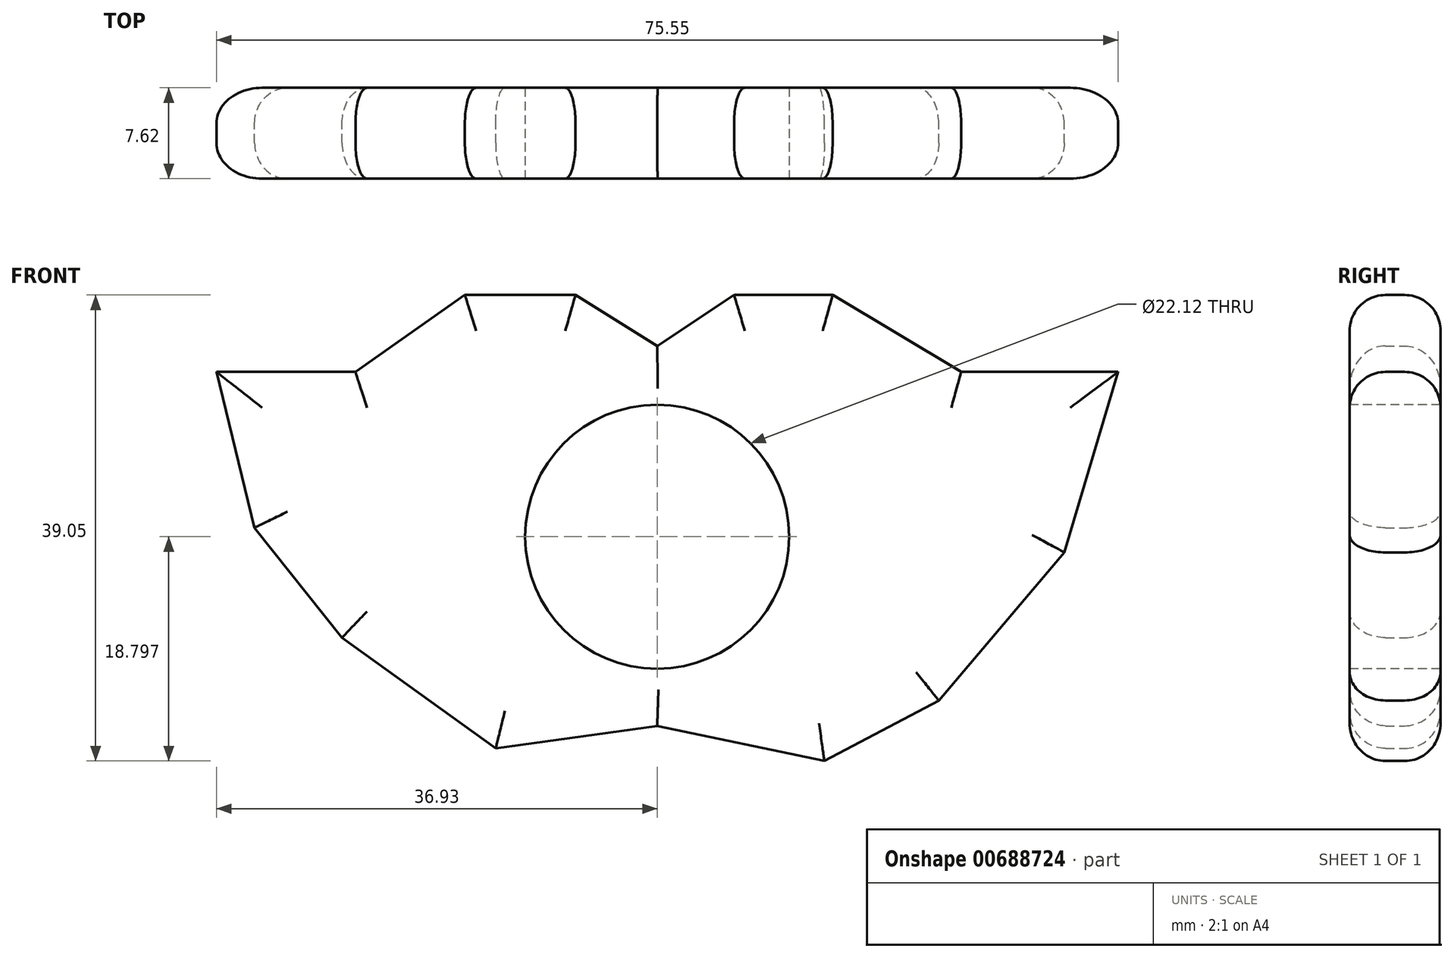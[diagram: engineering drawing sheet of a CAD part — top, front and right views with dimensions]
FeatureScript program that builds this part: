
annotation { "Feature Type Name" : "Feature", "Feature Type Description" : "" }
export const myFeature = defineFeature(function(context is Context, id is Id, definition is map)
    precondition{}
    {
        {
            var Q0;
            Q0=qCreatedBy(makeId("Front.planeOp"),FACE);
            var sketch = newSketch(context, id + "F0", { "sketchPlane" : qUnion([Q0])});
            skLineSegment(sketch, "E0", {"start": v(-6.84, 6.44) * mm, "end": v(0, 2.18) * mm});
            skLineSegment(sketch, "E1", {"start": v(0, 2.18) * mm, "end": v(6.44, 6.44) * mm});
            skLineSegment(sketch, "E2", {"start": v(-25.28, 0) * mm, "end": v(-36.93, 0) * mm});
            skLineSegment(sketch, "E3", {"start": v(-36.93, 0) * mm, "end": v(-33.74, -13.06) * mm});
            skLineSegment(sketch, "E4", {"start": v(-25.28, 0) * mm, "end": v(-16.12, 6.44) * mm});
            skLineSegment(sketch, "E5", {"start": v(-16.12, 6.44) * mm, "end": v(-6.84, 6.44) * mm});
            skLineSegment(sketch, "E6", {"start": v(6.44, 6.44) * mm, "end": v(14.7, 6.44) * mm});
            skLineSegment(sketch, "E7", {"start": v(14.7, 6.44) * mm, "end": v(25.47, 0) * mm});
            skLineSegment(sketch, "E8", {"start": v(38.62, 0) * mm, "end": v(34.11, -15.13) * mm});
            skLineSegment(sketch, "E9", {"start": v(-33.74, -13.06) * mm, "end": v(-26.4, -22.27) * mm});
            skLineSegment(sketch, "E10", {"start": v(-26.4, -22.27) * mm, "end": v(-13.54, -31.56) * mm});
            skLineSegment(sketch, "E11", {"start": v(34.11, -15.13) * mm, "end": v(23.59, -27.53) * mm});
            skLineSegment(sketch, "E12", {"start": v(23.59, -27.53) * mm, "end": v(14, -32.6) * mm});
            skLineSegment(sketch, "E13", {"start": v(14, -32.6) * mm, "end": v(0, -29.66) * mm});
            skLineSegment(sketch, "E14", {"start": v(0, -29.66) * mm, "end": v(-13.54, -31.56) * mm});
            skLineSegment(sketch, "E15", {"start": v(25.47, 0) * mm, "end": v(38.62, 0) * mm});
            skSolve(sketch);
        }
        {
            var Q0;
            Q0 = qSketchRegion(id + "F0", true);
            extrude(context, id + "F1", {"entities" : qUnion([Q0]), "depth" : 7.62 * mm, "offsetDistance" : 25.4 * mm});
        }
        {
            var Q0;
            Q0=makeQuery(id+"F1.opExtrude","CAP_FACE",FACE,{"disambiguationData":[OSD([sQuery(id+"F0.wireOp",EDGE,"E0"),sQuery(id+"F0.wireOp",EDGE,"E1"),sQuery(id+"F0.wireOp",EDGE,"E2"),sQuery(id+"F0.wireOp",EDGE,"E3"),sQuery(id+"F0.wireOp",EDGE,"E4"),sQuery(id+"F0.wireOp",EDGE,"E5"),sQuery(id+"F0.wireOp",EDGE,"E6"),sQuery(id+"F0.wireOp",EDGE,"E7"),sQuery(id+"F0.wireOp",EDGE,"bgftpzii-J6rh-5dA1-gnNM-FfCZ00Urv5oc"),sQuery(id+"F0.wireOp",EDGE,"E8"),sQuery(id+"F0.wireOp",EDGE,"E9"),sQuery(id+"F0.wireOp",EDGE,"E10"),sQuery(id+"F0.wireOp",EDGE,"E11"),sQuery(id+"F0.wireOp",EDGE,"E12"),sQuery(id+"F0.wireOp",EDGE,"E13"),sQuery(id+"F0.wireOp",EDGE,"E14")])],"isStart":false});
            var sketch = newSketch(context, id + "F2", { "sketchPlane" : qUnion([Q0])});
            skCircle(sketch, "E16", {"center": v(0, -13.81) * mm, "radius": 11.06 * mm});
            skCircle(sketch, "E17", {"center": v(0, -13.81) * mm, "radius": 13 * mm});
            skSolve(sketch);
        }
        {
            var Q0;
            Q0=makeQuery(id+"F2.imprint","IMPRINT",FACE,{"disambiguationData":[TD([[makeQuery(id+"F2.imprint","IMPRINT",EDGE,{"derivedFrom":sQuery(id+"F2.wireOp",EDGE,"E16")}),1.0]])]});
            extrude(context, id + "F3", {"entities" : qUnion([Q0]), "operationType" : NewBodyOperationType.REMOVE, "oppositeDirection" : true, "depth" : 10 * mm, "offsetDistance" : 25.4 * mm});
        }
        {
            var Q0;
            Q0=makeQuery(id+"F1.opExtrude","CAP_EDGE",EDGE,{"disambiguationData":[OSD([sQuery(id+"F0.wireOp",EDGE,"E3")])],"isStart":false});
            var Q1;
            Q1=makeQuery(id+"F1.opExtrude","CAP_EDGE",EDGE,{"disambiguationData":[OSD([sQuery(id+"F0.wireOp",EDGE,"E9")])],"isStart":false});
            var Q2;
            Q2=makeQuery(id+"F1.opExtrude","CAP_EDGE",EDGE,{"disambiguationData":[OSD([sQuery(id+"F0.wireOp",EDGE,"E10")])],"isStart":false});
            var Q3;
            Q3=makeQuery(id+"F1.opExtrude","CAP_EDGE",EDGE,{"disambiguationData":[OSD([sQuery(id+"F0.wireOp",EDGE,"E14")])],"isStart":false});
            var Q4;
            Q4=makeQuery(id+"F1.opExtrude","CAP_EDGE",EDGE,{"disambiguationData":[OSD([sQuery(id+"F0.wireOp",EDGE,"E13")])],"isStart":false});
            var Q5;
            Q5=makeQuery(id+"F1.opExtrude","CAP_EDGE",EDGE,{"disambiguationData":[OSD([sQuery(id+"F0.wireOp",EDGE,"E12")])],"isStart":false});
            var Q6;
            Q6=makeQuery(id+"F1.opExtrude","CAP_EDGE",EDGE,{"disambiguationData":[OSD([sQuery(id+"F0.wireOp",EDGE,"E11")])],"isStart":false});
            var Q7;
            Q7=makeQuery(id+"F1.opExtrude","CAP_EDGE",EDGE,{"disambiguationData":[OSD([sQuery(id+"F0.wireOp",EDGE,"E8")])],"isStart":false});
            var Q8;
            Q8=makeQuery(id+"F1.opExtrude","CAP_EDGE",EDGE,{"disambiguationData":[OSD([sQuery(id+"F0.wireOp",EDGE,"E15")])],"isStart":false});
            var Q9;
            Q9=makeQuery(id+"F1.opExtrude","CAP_EDGE",EDGE,{"disambiguationData":[OSD([sQuery(id+"F0.wireOp",EDGE,"E7")])],"isStart":false});
            var Q10;
            Q10=makeQuery(id+"F1.opExtrude","CAP_EDGE",EDGE,{"disambiguationData":[OSD([sQuery(id+"F0.wireOp",EDGE,"E6")])],"isStart":false});
            var Q11;
            Q11=makeQuery(id+"F1.opExtrude","CAP_EDGE",EDGE,{"disambiguationData":[OSD([sQuery(id+"F0.wireOp",EDGE,"E1")])],"isStart":false});
            var Q12;
            Q12=makeQuery(id+"F1.opExtrude","CAP_EDGE",EDGE,{"disambiguationData":[OSD([sQuery(id+"F0.wireOp",EDGE,"E0")])],"isStart":false});
            var Q13;
            Q13=makeQuery(id+"F1.opExtrude","CAP_EDGE",EDGE,{"disambiguationData":[OSD([sQuery(id+"F0.wireOp",EDGE,"E5")])],"isStart":false});
            var Q14;
            Q14=makeQuery(id+"F1.opExtrude","CAP_EDGE",EDGE,{"disambiguationData":[OSD([sQuery(id+"F0.wireOp",EDGE,"E4")])],"isStart":false});
            var Q15;
            Q15=makeQuery(id+"F1.opExtrude","CAP_EDGE",EDGE,{"disambiguationData":[OSD([sQuery(id+"F0.wireOp",EDGE,"E2")])],"isStart":false});
            var Q16;
            Q16=makeQuery(id+"F1.opExtrude","CAP_EDGE",EDGE,{"disambiguationData":[OSD([sQuery(id+"F0.wireOp",EDGE,"E2")])],"isStart":true});
            var Q17;
            Q17=makeQuery(id+"F1.opExtrude","CAP_EDGE",EDGE,{"disambiguationData":[OSD([sQuery(id+"F0.wireOp",EDGE,"E3")])],"isStart":true});
            var Q18;
            Q18=makeQuery(id+"F1.opExtrude","CAP_EDGE",EDGE,{"disambiguationData":[OSD([sQuery(id+"F0.wireOp",EDGE,"E9")])],"isStart":true});
            var Q19;
            Q19=makeQuery(id+"F1.opExtrude","CAP_EDGE",EDGE,{"disambiguationData":[OSD([sQuery(id+"F0.wireOp",EDGE,"E10")])],"isStart":true});
            var Q20;
            Q20=makeQuery(id+"F1.opExtrude","CAP_EDGE",EDGE,{"disambiguationData":[OSD([sQuery(id+"F0.wireOp",EDGE,"E14")])],"isStart":true});
            var Q21;
            Q21=makeQuery(id+"F1.opExtrude","CAP_EDGE",EDGE,{"disambiguationData":[OSD([sQuery(id+"F0.wireOp",EDGE,"E13")])],"isStart":true});
            var Q22;
            Q22=makeQuery(id+"F1.opExtrude","CAP_EDGE",EDGE,{"disambiguationData":[OSD([sQuery(id+"F0.wireOp",EDGE,"E12")])],"isStart":true});
            var Q23;
            Q23=makeQuery(id+"F1.opExtrude","CAP_EDGE",EDGE,{"disambiguationData":[OSD([sQuery(id+"F0.wireOp",EDGE,"E11")])],"isStart":true});
            var Q24;
            Q24=makeQuery(id+"F1.opExtrude","CAP_EDGE",EDGE,{"disambiguationData":[OSD([sQuery(id+"F0.wireOp",EDGE,"E8")])],"isStart":true});
            var Q25;
            Q25=makeQuery(id+"F1.opExtrude","CAP_EDGE",EDGE,{"disambiguationData":[OSD([sQuery(id+"F0.wireOp",EDGE,"E15")])],"isStart":true});
            var Q26;
            Q26=makeQuery(id+"F1.opExtrude","CAP_EDGE",EDGE,{"disambiguationData":[OSD([sQuery(id+"F0.wireOp",EDGE,"E7")])],"isStart":true});
            var Q27;
            Q27=makeQuery(id+"F1.opExtrude","CAP_EDGE",EDGE,{"disambiguationData":[OSD([sQuery(id+"F0.wireOp",EDGE,"E6")])],"isStart":true});
            var Q28;
            Q28=makeQuery(id+"F1.opExtrude","CAP_EDGE",EDGE,{"disambiguationData":[OSD([sQuery(id+"F0.wireOp",EDGE,"E1")])],"isStart":true});
            var Q29;
            Q29=makeQuery(id+"F1.opExtrude","CAP_EDGE",EDGE,{"disambiguationData":[OSD([sQuery(id+"F0.wireOp",EDGE,"E0")])],"isStart":true});
            var Q30;
            Q30=makeQuery(id+"F1.opExtrude","CAP_EDGE",EDGE,{"disambiguationData":[OSD([sQuery(id+"F0.wireOp",EDGE,"E5")])],"isStart":true});
            var Q31;
            Q31=makeQuery(id+"F1.opExtrude","CAP_EDGE",EDGE,{"disambiguationData":[OSD([sQuery(id+"F0.wireOp",EDGE,"E4")])],"isStart":true});
            fillet(context, id + "F4", {"entities" : qUnion([Q0, Q1, Q2, Q3, Q4, Q5, Q6, Q7, Q8, Q9, Q10, Q11, Q12, Q13, Q14, Q15, Q16, Q17, Q18, Q19, Q20, Q21, Q22, Q23, Q24, Q25, Q26, Q27, Q28, Q29, Q30, Q31]), "radius" : 3 * mm, "tangentPropagation" : true, "allowEdgeOverflow" : false});
        }
    });
